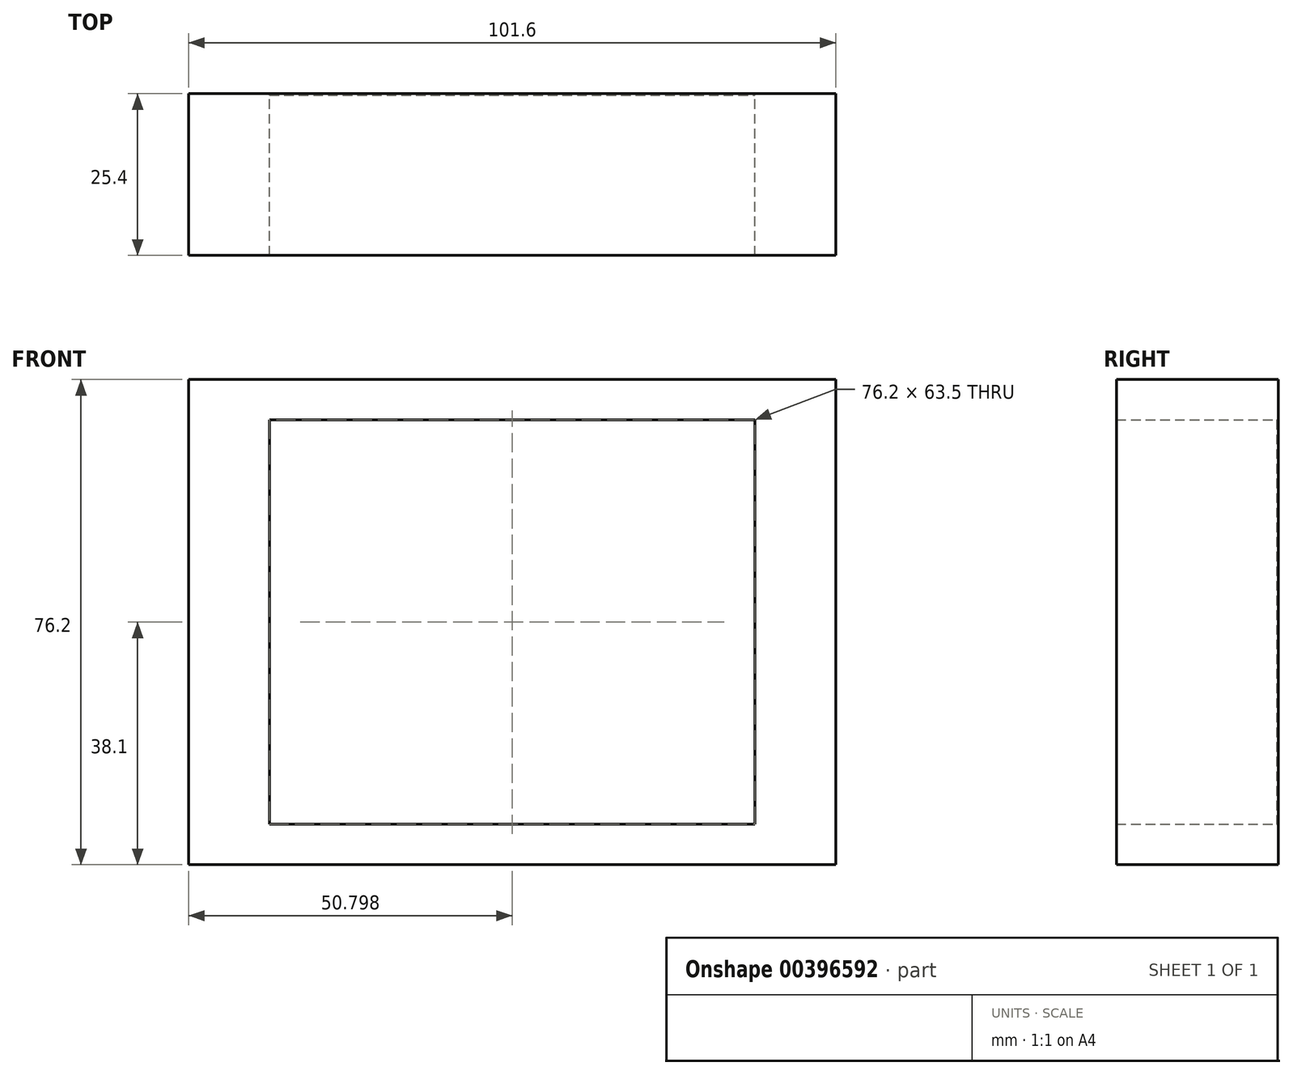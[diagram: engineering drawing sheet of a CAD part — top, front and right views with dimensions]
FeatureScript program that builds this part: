
annotation { "Feature Type Name" : "Feature", "Feature Type Description" : "" }
export const myFeature = defineFeature(function(context is Context, id is Id, definition is map)
    precondition{}
    {
        {
            var Q0;
            Q0=qCreatedBy(makeId("Front.planeOp"),FACE);
            var sketch = newSketch(context, id + "F0", { "sketchPlane" : qUnion([Q0])});
            skLineSegment(sketch, "E0.bottom", {"start": v(-53.3, 45.42) * mm, "end": v(48.3, 45.42) * mm});
            skLineSegment(sketch, "E0.top", {"start": v(-53.3, -30.78) * mm, "end": v(48.3, -30.78) * mm});
            skLineSegment(sketch, "E0.left", {"start": v(-53.3, 45.42) * mm, "end": v(-53.3, -30.78) * mm});
            skLineSegment(sketch, "E0.right", {"start": v(48.3, 45.42) * mm, "end": v(48.3, -30.78) * mm});
            skLineSegment(sketch, "E1.bottom", {"start": v(-40.6, 39.07) * mm, "end": v(35.6, 39.07) * mm});
            skLineSegment(sketch, "E1.top", {"start": v(-40.6, -24.43) * mm, "end": v(35.6, -24.43) * mm});
            skLineSegment(sketch, "E1.left", {"start": v(-40.6, 39.07) * mm, "end": v(-40.6, -24.43) * mm});
            skLineSegment(sketch, "E1.right", {"start": v(35.6, 39.07) * mm, "end": v(35.6, -24.43) * mm});
            skSolve(sketch);
        }
        {
            var Q0;
            Q0 = qSketchRegion(id + "F0", true);
            extrude(context, id + "F1", {"entities" : qUnion([Q0]), "depth" : 25.4 * mm});
        }
        {
            var Q0;
            Q0=makeQuery(id+"F0.imprint","IMPRINT",FACE,{"disambiguationData":[TD([[makeQuery(id+"F0.imprint","IMPRINT",EDGE,{"derivedFrom":sQuery(id+"F0.wireOp",EDGE,"E1.bottom")}),-1.0]])]});
            extrude(context, id + "F2", {"entities" : qUnion([Q0]), "depth" : 0.25 * mm});
        }
    });
